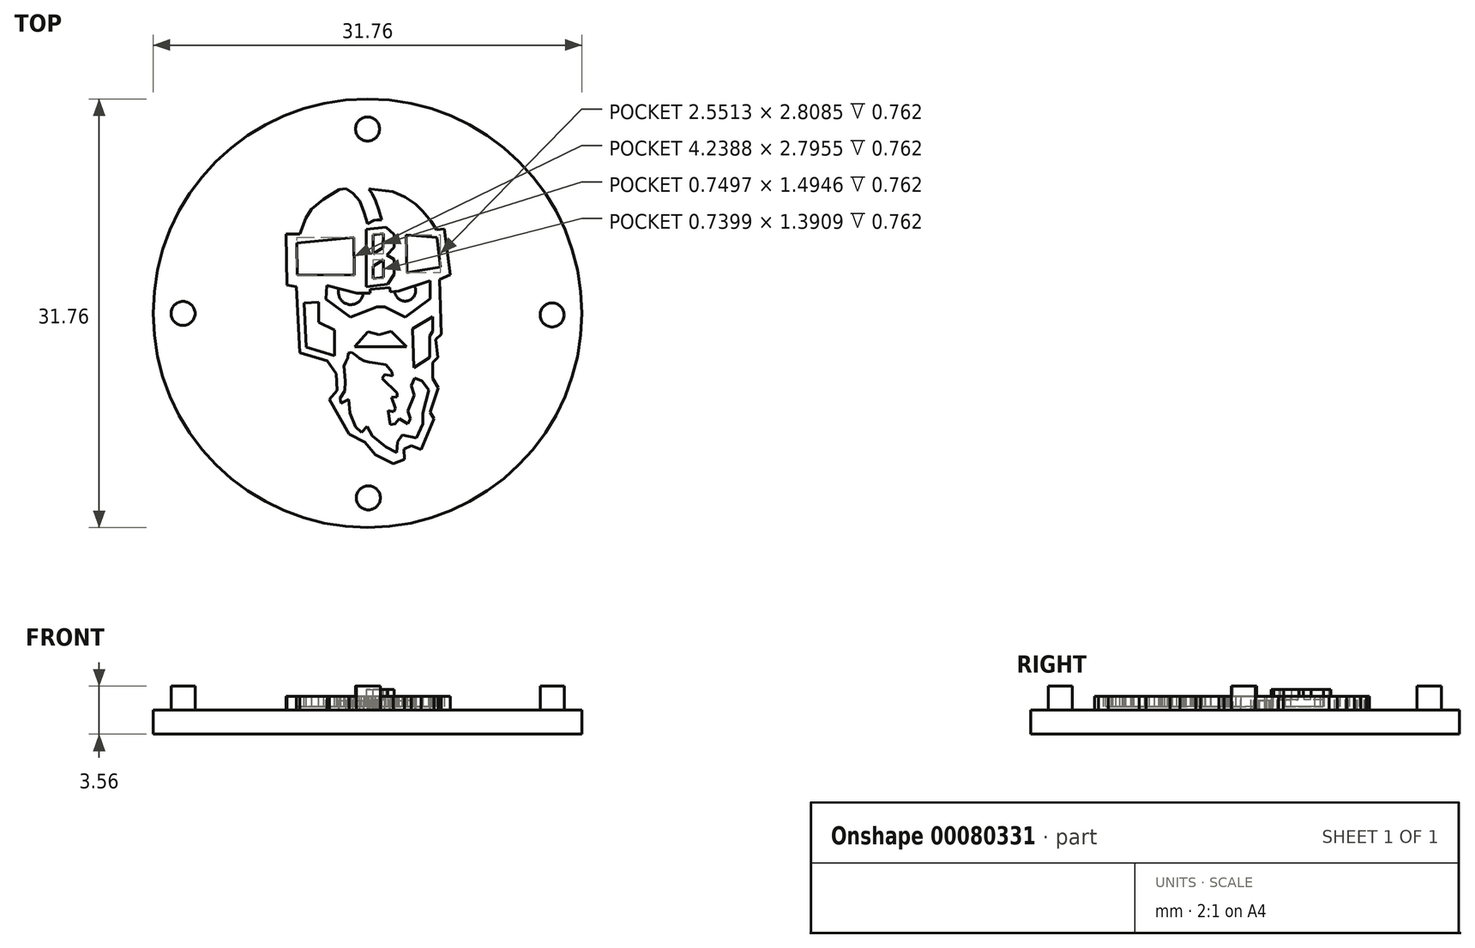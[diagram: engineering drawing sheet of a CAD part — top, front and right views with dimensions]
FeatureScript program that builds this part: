
annotation { "Feature Type Name" : "Feature", "Feature Type Description" : "" }
export const myFeature = defineFeature(function(context is Context, id is Id, definition is map)
    precondition{}
    {
        {
            var Q0;
            Q0=qCreatedBy(makeId("Top.planeOp"),FACE);
            var sketch = newSketch(context, id + "F0", { "sketchPlane" : qUnion([Q0])});
            skCircle(sketch, "E0", {"center": v(0, 0) * mm, "radius": 15.88 * mm});
            skSolve(sketch);
        }
        {
            var Q0;
            Q0=qSketchRegion(id+"F0",true);
            extrude(context, id + "F1", {"entities" : qUnion([Q0]), "oppositeDirection" : true, "depth" : 1.78 * mm});
        }
        {
            var Q0;
            Q0=makeQuery(id+"F1.opExtrude","CAP_FACE",FACE,{"disambiguationData":[OSD([sQuery(id+"F0.wireOp",EDGE,"E0")])],"isStart":true});
            var sketch = newSketch(context, id + "F2", { "sketchPlane" : qUnion([Q0])});
            skCircle(sketch, "E1", {"center": v(0, 0) * mm, "radius": 12.7 * mm});
            skSolve(sketch);
        }
        {
            var Q0;
            Q0=makeQuery(id+"F2.imprint","IMPRINT",FACE,{"disambiguationData":[TD([[makeQuery(id+"F2.imprint","IMPRINT",EDGE,{"derivedFrom":sQuery(id+"F2.wireOp",EDGE,"E1")}),-1.0]])]});
            var sketch = newSketch(context, id + "F3", { "sketchPlane" : qUnion([Q0])});
            skCircle(sketch, "E2", {"center": v(0, 13.65) * mm, "radius": 0.89 * mm});
            skCircle(sketch, "E3", {"center": v(-13.66, -0.02) * mm, "radius": 0.89 * mm});
            skCircle(sketch, "E4", {"center": v(0.06, -13.68) * mm, "radius": 0.89 * mm});
            skCircle(sketch, "E5", {"center": v(13.67, -0.12) * mm, "radius": 0.89 * mm});
            skSolve(sketch);
        }
        {
            var Q0;
            Q0=qSketchRegion(id+"F3",true);
            extrude(context, id + "F4", {"entities" : qUnion([Q0]), "operationType" : NewBodyOperationType.ADD, "depth" : 1.78 * mm});
        }
        {
            var Q0;
            Q0=makeQuery(id+"F2.imprint","IMPRINT",FACE,{"disambiguationData":[TD([[makeQuery(id+"F2.imprint","IMPRINT",EDGE,{"derivedFrom":sQuery(id+"F2.wireOp",EDGE,"E1")}),-1.0]])]});
            var sketch = newSketch(context, id + "F5", { "sketchPlane" : qUnion([Q0])});
            skLineSegment(sketch, "E6", {"start": v(-5.97, 2.09) * mm, "end": v(-6.04, 5.87) * mm});
            skLineSegment(sketch, "E7", {"start": v(-6.04, 5.87) * mm, "end": v(-5.01, 5.87) * mm});
            skLineSegment(sketch, "E8", {"start": v(-5.01, 5.87) * mm, "end": v(-4.57, 7.04) * mm});
            skLineSegment(sketch, "E9", {"start": v(-4.57, 7.04) * mm, "end": v(-4.15, 7.72) * mm});
            skLineSegment(sketch, "E10", {"start": v(-4.15, 7.72) * mm, "end": v(-3.26, 8.45) * mm});
            skLineSegment(sketch, "E11", {"start": v(-3.26, 8.45) * mm, "end": v(-2.1, 9.17) * mm});
            skLineSegment(sketch, "E12", {"start": v(-2.1, 9.17) * mm, "end": v(-1.1, 9.3) * mm});
            skLineSegment(sketch, "E13", {"start": v(-1.1, 9.3) * mm, "end": v(0.25, 9.2) * mm});
            skLineSegment(sketch, "E14", {"start": v(0.25, 9.2) * mm, "end": v(1.86, 9) * mm});
            skLineSegment(sketch, "E15", {"start": v(1.86, 9) * mm, "end": v(2.79, 8.58) * mm});
            skLineSegment(sketch, "E16", {"start": v(2.79, 8.58) * mm, "end": v(3.55, 8.1) * mm});
            skLineSegment(sketch, "E17", {"start": v(3.55, 8.1) * mm, "end": v(4.1, 7.55) * mm});
            skLineSegment(sketch, "E18", {"start": v(4.1, 7.55) * mm, "end": v(4.71, 6.83) * mm});
            skLineSegment(sketch, "E19", {"start": v(4.71, 6.83) * mm, "end": v(5.13, 6.18) * mm});
            skLineSegment(sketch, "E20", {"start": v(5.13, 6.18) * mm, "end": v(5.68, 6.25) * mm});
            skLineSegment(sketch, "E21", {"start": v(5.68, 6.25) * mm, "end": v(6.12, 2.84) * mm});
            skLineSegment(sketch, "E22", {"start": v(6.12, 2.84) * mm, "end": v(5.33, 2.5) * mm});
            skLineSegment(sketch, "E23", {"start": v(5.47, -1.56) * mm, "end": v(5.06, -1.93) * mm});
            skLineSegment(sketch, "E24", {"start": v(5.06, -1.93) * mm, "end": v(5.2, -3.27) * mm});
            skLineSegment(sketch, "E25", {"start": v(5.2, -3.27) * mm, "end": v(4.82, -3.65) * mm});
            skLineSegment(sketch, "E26", {"start": v(4.82, -3.65) * mm, "end": v(4.82, -4.82) * mm});
            skLineSegment(sketch, "E27", {"start": v(4.82, -4.82) * mm, "end": v(5.23, -5.54) * mm});
            skLineSegment(sketch, "E28", {"start": v(5.23, -5.54) * mm, "end": v(4.65, -7.33) * mm});
            skLineSegment(sketch, "E29", {"start": v(4.65, -7.33) * mm, "end": v(4.92, -7.81) * mm});
            skLineSegment(sketch, "E30", {"start": v(4.92, -7.81) * mm, "end": v(3.96, -10.11) * mm});
            skLineSegment(sketch, "E31", {"start": v(3.96, -10.11) * mm, "end": v(3.24, -9.8) * mm});
            skLineSegment(sketch, "E32", {"start": v(3.24, -9.8) * mm, "end": v(2.69, -10.08) * mm});
            skLineSegment(sketch, "E33", {"start": v(2.69, -10.08) * mm, "end": v(2.72, -10.84) * mm});
            skLineSegment(sketch, "E34", {"start": v(2.72, -10.84) * mm, "end": v(1.9, -11.15) * mm});
            skLineSegment(sketch, "E35", {"start": v(1.9, -11.15) * mm, "end": v(0.59, -10.5) * mm});
            skLineSegment(sketch, "E36", {"start": v(0.59, -10.5) * mm, "end": v(-0.2, -9.56) * mm});
            skLineSegment(sketch, "E37", {"start": v(-0.2, -9.56) * mm, "end": v(-1.37, -8.95) * mm});
            skLineSegment(sketch, "E38", {"start": v(-1.37, -8.95) * mm, "end": v(-2.81, -6.4) * mm});
            skLineSegment(sketch, "E39", {"start": v(-2.81, -6.4) * mm, "end": v(-2.26, -5.71) * mm});
            skLineSegment(sketch, "E40", {"start": v(-2.26, -5.71) * mm, "end": v(-2.33, -4.48) * mm});
            skLineSegment(sketch, "E41", {"start": v(-2.33, -4.48) * mm, "end": v(-2.98, -3.52) * mm});
            skLineSegment(sketch, "E42", {"start": v(-2.98, -3.52) * mm, "end": v(-5.01, -2.93) * mm});
            skLineSegment(sketch, "E43", {"start": v(-5.25, 1.95) * mm, "end": v(-5.97, 2.09) * mm});
            skLineSegment(sketch, "E44", {"start": v(-5.25, 1.95) * mm, "end": v(-5.01, -2.93) * mm});
            skLineSegment(sketch, "E45", {"start": v(5.33, 2.5) * mm, "end": v(5.47, -1.56) * mm});
            skSolve(sketch);
        }
        {
            var Q0;
            Q0=qSketchRegion(id+"F5",true);
            extrude(context, id + "F6", {"entities" : qUnion([Q0]), "operationType" : NewBodyOperationType.ADD, "depth" : 1.02 * mm});
        }
        {
            var Q0;
            Q0=makeQuery(id+"F6.opExtrude","CAP_FACE",FACE,{"disambiguationData":[OSD([sQuery(id+"F5.wireOp",EDGE,"E6"),sQuery(id+"F5.wireOp",EDGE,"E7"),sQuery(id+"F5.wireOp",EDGE,"E8"),sQuery(id+"F5.wireOp",EDGE,"E9"),sQuery(id+"F5.wireOp",EDGE,"E10"),sQuery(id+"F5.wireOp",EDGE,"E11"),sQuery(id+"F5.wireOp",EDGE,"E12"),sQuery(id+"F5.wireOp",EDGE,"E13"),sQuery(id+"F5.wireOp",EDGE,"E14"),sQuery(id+"F5.wireOp",EDGE,"E15"),sQuery(id+"F5.wireOp",EDGE,"E16"),sQuery(id+"F5.wireOp",EDGE,"E17"),sQuery(id+"F5.wireOp",EDGE,"E18"),sQuery(id+"F5.wireOp",EDGE,"E19"),sQuery(id+"F5.wireOp",EDGE,"E20"),sQuery(id+"F5.wireOp",EDGE,"E21"),sQuery(id+"F5.wireOp",EDGE,"E22"),sQuery(id+"F5.wireOp",EDGE,"E23"),sQuery(id+"F5.wireOp",EDGE,"E24"),sQuery(id+"F5.wireOp",EDGE,"E25"),sQuery(id+"F5.wireOp",EDGE,"E26"),sQuery(id+"F5.wireOp",EDGE,"E27"),sQuery(id+"F5.wireOp",EDGE,"E28"),sQuery(id+"F5.wireOp",EDGE,"E29"),sQuery(id+"F5.wireOp",EDGE,"E30"),sQuery(id+"F5.wireOp",EDGE,"E31"),sQuery(id+"F5.wireOp",EDGE,"E32"),sQuery(id+"F5.wireOp",EDGE,"E33"),sQuery(id+"F5.wireOp",EDGE,"E34"),sQuery(id+"F5.wireOp",EDGE,"E35"),sQuery(id+"F5.wireOp",EDGE,"E36"),sQuery(id+"F5.wireOp",EDGE,"E37"),sQuery(id+"F5.wireOp",EDGE,"E38"),sQuery(id+"F5.wireOp",EDGE,"E39"),sQuery(id+"F5.wireOp",EDGE,"E40"),sQuery(id+"F5.wireOp",EDGE,"E41"),sQuery(id+"F5.wireOp",EDGE,"E42"),sQuery(id+"F5.wireOp",EDGE,"E43"),sQuery(id+"F5.wireOp",EDGE,"E44"),sQuery(id+"F5.wireOp",EDGE,"E45")])],"isStart":false});
            var sketch = newSketch(context, id + "F7", { "sketchPlane" : qUnion([Q0])});
            skLineSegment(sketch, "E46", {"start": v(1.35, 6.38) * mm, "end": v(-0.1, 6.21) * mm});
            skLineSegment(sketch, "E47", {"start": v(-0.1, 6.21) * mm, "end": v(-0.1, 1.96) * mm});
            skLineSegment(sketch, "E48", {"start": v(1.99, 2.88) * mm, "end": v(1.99, 4) * mm});
            skLineSegment(sketch, "E49", {"start": v(1.98, 4.9) * mm, "end": v(1.98, 5.82) * mm});
            skLineSegment(sketch, "E50", {"start": v(1.98, 5.82) * mm, "end": v(1.35, 6.38) * mm});
            skLineSegment(sketch, "E51", {"start": v(1.99, 4) * mm, "end": v(1.44, 4.32) * mm});
            skLineSegment(sketch, "E52", {"start": v(1.44, 4.32) * mm, "end": v(1.98, 4.9) * mm});
            skLineSegment(sketch, "E53", {"start": v(-0.1, 1.96) * mm, "end": v(1.5, 2.15) * mm});
            skLineSegment(sketch, "E54", {"start": v(1.5, 2.15) * mm, "end": v(1.99, 2.88) * mm});
            skSolve(sketch);
        }
        {
            var Q0;
            Q0=qSketchRegion(id+"F7",true);
            extrude(context, id + "F8", {"entities" : qUnion([Q0]), "operationType" : NewBodyOperationType.ADD, "depth" : 0.5 * mm});
        }
        {
            var Q0;
            Q0=makeQuery(id+"F6.opExtrude","CAP_FACE",FACE,{"disambiguationData":[OSD([sQuery(id+"F5.wireOp",EDGE,"E6"),sQuery(id+"F5.wireOp",EDGE,"E7"),sQuery(id+"F5.wireOp",EDGE,"E8"),sQuery(id+"F5.wireOp",EDGE,"E9"),sQuery(id+"F5.wireOp",EDGE,"E10"),sQuery(id+"F5.wireOp",EDGE,"E11"),sQuery(id+"F5.wireOp",EDGE,"E12"),sQuery(id+"F5.wireOp",EDGE,"E13"),sQuery(id+"F5.wireOp",EDGE,"E14"),sQuery(id+"F5.wireOp",EDGE,"E15"),sQuery(id+"F5.wireOp",EDGE,"E16"),sQuery(id+"F5.wireOp",EDGE,"E17"),sQuery(id+"F5.wireOp",EDGE,"E18"),sQuery(id+"F5.wireOp",EDGE,"E19"),sQuery(id+"F5.wireOp",EDGE,"E20"),sQuery(id+"F5.wireOp",EDGE,"E21"),sQuery(id+"F5.wireOp",EDGE,"E22"),sQuery(id+"F5.wireOp",EDGE,"E23"),sQuery(id+"F5.wireOp",EDGE,"E24"),sQuery(id+"F5.wireOp",EDGE,"E25"),sQuery(id+"F5.wireOp",EDGE,"E26"),sQuery(id+"F5.wireOp",EDGE,"E27"),sQuery(id+"F5.wireOp",EDGE,"E28"),sQuery(id+"F5.wireOp",EDGE,"E29"),sQuery(id+"F5.wireOp",EDGE,"E30"),sQuery(id+"F5.wireOp",EDGE,"E31"),sQuery(id+"F5.wireOp",EDGE,"E32"),sQuery(id+"F5.wireOp",EDGE,"E33"),sQuery(id+"F5.wireOp",EDGE,"E34"),sQuery(id+"F5.wireOp",EDGE,"E35"),sQuery(id+"F5.wireOp",EDGE,"E36"),sQuery(id+"F5.wireOp",EDGE,"E37"),sQuery(id+"F5.wireOp",EDGE,"E38"),sQuery(id+"F5.wireOp",EDGE,"E39"),sQuery(id+"F5.wireOp",EDGE,"E40"),sQuery(id+"F5.wireOp",EDGE,"E41"),sQuery(id+"F5.wireOp",EDGE,"E42"),sQuery(id+"F5.wireOp",EDGE,"E43"),sQuery(id+"F5.wireOp",EDGE,"E44"),sQuery(id+"F5.wireOp",EDGE,"E45")])],"isStart":false});
            var sketch = newSketch(context, id + "F9", { "sketchPlane" : qUnion([Q0])});
            skLineSegment(sketch, "E55", {"start": v(-5.23, 5.2) * mm, "end": v(-5.2, 2.85) * mm});
            skLineSegment(sketch, "E56", {"start": v(-5.2, 2.85) * mm, "end": v(-1, 2.8) * mm});
            skLineSegment(sketch, "E57", {"start": v(-1, 2.8) * mm, "end": v(-1, 5.6) * mm});
            skLineSegment(sketch, "E58", {"start": v(-1, 5.6) * mm, "end": v(-5.23, 5.2) * mm});
            skLineSegment(sketch, "E59", {"start": v(2.86, 5.8) * mm, "end": v(5.14, 5.6) * mm});
            skLineSegment(sketch, "E60", {"start": v(5.14, 5.6) * mm, "end": v(5.41, 3.42) * mm});
            skLineSegment(sketch, "E61", {"start": v(5.41, 3.42) * mm, "end": v(2.93, 3) * mm});
            skLineSegment(sketch, "E62", {"start": v(2.93, 3) * mm, "end": v(2.86, 5.8) * mm});
            skSolve(sketch);
        }
        {
            var Q0;
            Q0=qSketchRegion(id+"F9",true);
            extrude(context, id + "F10", {"entities" : qUnion([Q0]), "operationType" : NewBodyOperationType.REMOVE, "oppositeDirection" : true, "depth" : 0.76 * mm});
        }
        {
            var Q0;
            Q0=makeQuery(id+"F6.opExtrude","CAP_FACE",FACE,{"disambiguationData":[OSD([sQuery(id+"F5.wireOp",EDGE,"E6"),sQuery(id+"F5.wireOp",EDGE,"E7"),sQuery(id+"F5.wireOp",EDGE,"E8"),sQuery(id+"F5.wireOp",EDGE,"E9"),sQuery(id+"F5.wireOp",EDGE,"E10"),sQuery(id+"F5.wireOp",EDGE,"E11"),sQuery(id+"F5.wireOp",EDGE,"E12"),sQuery(id+"F5.wireOp",EDGE,"E13"),sQuery(id+"F5.wireOp",EDGE,"E14"),sQuery(id+"F5.wireOp",EDGE,"E15"),sQuery(id+"F5.wireOp",EDGE,"E16"),sQuery(id+"F5.wireOp",EDGE,"E17"),sQuery(id+"F5.wireOp",EDGE,"E18"),sQuery(id+"F5.wireOp",EDGE,"E19"),sQuery(id+"F5.wireOp",EDGE,"E20"),sQuery(id+"F5.wireOp",EDGE,"E21"),sQuery(id+"F5.wireOp",EDGE,"E22"),sQuery(id+"F5.wireOp",EDGE,"E23"),sQuery(id+"F5.wireOp",EDGE,"E24"),sQuery(id+"F5.wireOp",EDGE,"E25"),sQuery(id+"F5.wireOp",EDGE,"E26"),sQuery(id+"F5.wireOp",EDGE,"E27"),sQuery(id+"F5.wireOp",EDGE,"E28"),sQuery(id+"F5.wireOp",EDGE,"E29"),sQuery(id+"F5.wireOp",EDGE,"E30"),sQuery(id+"F5.wireOp",EDGE,"E31"),sQuery(id+"F5.wireOp",EDGE,"E32"),sQuery(id+"F5.wireOp",EDGE,"E33"),sQuery(id+"F5.wireOp",EDGE,"E34"),sQuery(id+"F5.wireOp",EDGE,"E35"),sQuery(id+"F5.wireOp",EDGE,"E36"),sQuery(id+"F5.wireOp",EDGE,"E37"),sQuery(id+"F5.wireOp",EDGE,"E38"),sQuery(id+"F5.wireOp",EDGE,"E39"),sQuery(id+"F5.wireOp",EDGE,"E40"),sQuery(id+"F5.wireOp",EDGE,"E41"),sQuery(id+"F5.wireOp",EDGE,"E42"),sQuery(id+"F5.wireOp",EDGE,"E43"),sQuery(id+"F5.wireOp",EDGE,"E44"),sQuery(id+"F5.wireOp",EDGE,"E45")])],"isStart":false});
            var sketch = newSketch(context, id + "F11", { "sketchPlane" : qUnion([Q0])});
            skLineSegment(sketch, "E63", {"start": v(-3.03, 2.07) * mm, "end": v(-0.78, 1.48) * mm});
            skLineSegment(sketch, "E64", {"start": v(-0.78, 1.48) * mm, "end": v(0.2, 1.48) * mm});
            skLineSegment(sketch, "E65", {"start": v(0.2, 1.48) * mm, "end": v(0.2, 1.78) * mm});
            skLineSegment(sketch, "E66", {"start": v(0.2, 1.78) * mm, "end": v(1.65, 1.9) * mm});
            skLineSegment(sketch, "E67", {"start": v(1.65, 1.9) * mm, "end": v(1.68, 1.58) * mm});
            skLineSegment(sketch, "E68", {"start": v(1.68, 1.58) * mm, "end": v(2.32, 1.63) * mm});
            skLineSegment(sketch, "E69", {"start": v(2.32, 1.63) * mm, "end": v(4.64, 2.4) * mm});
            skLineSegment(sketch, "E70", {"start": v(4.64, 2.4) * mm, "end": v(4.64, 1.09) * mm});
            skLineSegment(sketch, "E71", {"start": v(4.64, 1.09) * mm, "end": v(2.8, -0.3) * mm});
            skLineSegment(sketch, "E72", {"start": v(2.8, -0.3) * mm, "end": v(1.27, 0.46) * mm});
            skLineSegment(sketch, "E73", {"start": v(0.7, 0.46) * mm, "end": v(-1.26, -0.3) * mm});
            skLineSegment(sketch, "E74", {"start": v(-1.26, -0.3) * mm, "end": v(-3.08, 1.04) * mm});
            skLineSegment(sketch, "E75", {"start": v(-3.08, 1.04) * mm, "end": v(-3.03, 2.07) * mm});
            skLineSegment(sketch, "E76", {"start": v(0.7, 0.46) * mm, "end": v(1.27, 0.46) * mm});
            skSolve(sketch);
        }
        {
            var Q0;
            Q0=qSketchRegion(id+"F11",true);
            extrude(context, id + "F12", {"entities" : qUnion([Q0]), "operationType" : NewBodyOperationType.REMOVE, "oppositeDirection" : true, "depth" : 1.02 * mm});
        }
        {
            var Q0;
            Q0=makeQuery(id+"F2.imprint","IMPRINT",FACE,{"disambiguationData":[TD([[makeQuery(id+"F2.imprint","IMPRINT",EDGE,{"derivedFrom":sQuery(id+"F2.wireOp",EDGE,"E1")}),1.0]])]});
            var sketch = newSketch(context, id + "F13", { "sketchPlane" : qUnion([Q0])});
            skLineSegment(sketch, "E77", {"start": v(-2.11, 1.83) * mm, "end": v(-0.78, 1.48) * mm});
            skLineSegment(sketch, "E78", {"start": v(-0.78, 1.48) * mm, "end": v(-0.32, 1.48) * mm});
            skArc(sketch, "E79", {"start": v(-2.11, 1.83) * mm, "mid": v(-1.41, 0.65) * mm, "end": v(-0.32, 1.48) * mm});
            skLineSegment(sketch, "E80", {"start": v(3.48, 2.02) * mm, "end": v(2.32, 1.63) * mm});
            skLineSegment(sketch, "E81", {"start": v(2.32, 1.63) * mm, "end": v(2.02, 1.6) * mm});
            skArc(sketch, "E82", {"start": v(2.02, 1.6) * mm, "mid": v(3, 0.92) * mm, "end": v(3.48, 2.02) * mm});
            skSolve(sketch);
        }
        {
            var Q0;
            Q0=qSketchRegion(id+"F13",true);
            extrude(context, id + "F14", {"entities" : qUnion([Q0]), "operationType" : NewBodyOperationType.ADD, "depth" : 0.71 * mm});
        }
        {
            var Q0;
            Q0=makeQuery(id+"F6.opExtrude","CAP_FACE",FACE,{"disambiguationData":[OSD([sQuery(id+"F5.wireOp",EDGE,"E6"),sQuery(id+"F5.wireOp",EDGE,"E7"),sQuery(id+"F5.wireOp",EDGE,"E8"),sQuery(id+"F5.wireOp",EDGE,"E9"),sQuery(id+"F5.wireOp",EDGE,"E10"),sQuery(id+"F5.wireOp",EDGE,"E11"),sQuery(id+"F5.wireOp",EDGE,"E12"),sQuery(id+"F5.wireOp",EDGE,"E13"),sQuery(id+"F5.wireOp",EDGE,"E14"),sQuery(id+"F5.wireOp",EDGE,"E15"),sQuery(id+"F5.wireOp",EDGE,"E16"),sQuery(id+"F5.wireOp",EDGE,"E17"),sQuery(id+"F5.wireOp",EDGE,"E18"),sQuery(id+"F5.wireOp",EDGE,"E19"),sQuery(id+"F5.wireOp",EDGE,"E20"),sQuery(id+"F5.wireOp",EDGE,"E21"),sQuery(id+"F5.wireOp",EDGE,"E22"),sQuery(id+"F5.wireOp",EDGE,"E23"),sQuery(id+"F5.wireOp",EDGE,"E24"),sQuery(id+"F5.wireOp",EDGE,"E25"),sQuery(id+"F5.wireOp",EDGE,"E26"),sQuery(id+"F5.wireOp",EDGE,"E27"),sQuery(id+"F5.wireOp",EDGE,"E28"),sQuery(id+"F5.wireOp",EDGE,"E29"),sQuery(id+"F5.wireOp",EDGE,"E30"),sQuery(id+"F5.wireOp",EDGE,"E31"),sQuery(id+"F5.wireOp",EDGE,"E32"),sQuery(id+"F5.wireOp",EDGE,"E33"),sQuery(id+"F5.wireOp",EDGE,"E34"),sQuery(id+"F5.wireOp",EDGE,"E35"),sQuery(id+"F5.wireOp",EDGE,"E36"),sQuery(id+"F5.wireOp",EDGE,"E37"),sQuery(id+"F5.wireOp",EDGE,"E38"),sQuery(id+"F5.wireOp",EDGE,"E39"),sQuery(id+"F5.wireOp",EDGE,"E40"),sQuery(id+"F5.wireOp",EDGE,"E41"),sQuery(id+"F5.wireOp",EDGE,"E42"),sQuery(id+"F5.wireOp",EDGE,"E43"),sQuery(id+"F5.wireOp",EDGE,"E44"),sQuery(id+"F5.wireOp",EDGE,"E45")])],"isStart":false});
            var sketch = newSketch(context, id + "F15", { "sketchPlane" : qUnion([Q0])});
            skLineSegment(sketch, "E83", {"start": v(-4.69, 0.77) * mm, "end": v(-4.52, -2.51) * mm});
            skLineSegment(sketch, "E84", {"start": v(-4.52, -2.51) * mm, "end": v(-2.46, -3.14) * mm});
            skLineSegment(sketch, "E85", {"start": v(-2.46, -3.14) * mm, "end": v(-2.46, -1.26) * mm});
            skLineSegment(sketch, "E86", {"start": v(-2.46, -1.26) * mm, "end": v(-3.63, -0.66) * mm});
            skLineSegment(sketch, "E87", {"start": v(-3.63, -0.66) * mm, "end": v(-3.63, 0.83) * mm});
            skLineSegment(sketch, "E88", {"start": v(-3.63, 0.83) * mm, "end": v(-4.69, 0.77) * mm});
            skLineSegment(sketch, "E89", {"start": v(4.84, -0.26) * mm, "end": v(4.84, -1.35) * mm});
            skLineSegment(sketch, "E90", {"start": v(4.84, -1.35) * mm, "end": v(4.6, -1.69) * mm});
            skLineSegment(sketch, "E91", {"start": v(4.6, -1.69) * mm, "end": v(4.6, -3.29) * mm});
            skLineSegment(sketch, "E92", {"start": v(4.6, -3.29) * mm, "end": v(3.44, -4.02) * mm});
            skLineSegment(sketch, "E93", {"start": v(3.34, -1.14) * mm, "end": v(4.84, -0.26) * mm});
            skLineSegment(sketch, "E94", {"start": v(3.34, -1.14) * mm, "end": v(3.44, -4.02) * mm});
            skSolve(sketch);
        }
        {
            var Q0;
            Q0=qSketchRegion(id+"F15",true);
            extrude(context, id + "F16", {"entities" : qUnion([Q0]), "operationType" : NewBodyOperationType.REMOVE, "oppositeDirection" : true, "depth" : 0.76 * mm});
        }
        {
            var Q0;
            Q0=makeQuery(id+"F6.opExtrude","CAP_FACE",FACE,{"disambiguationData":[OSD([sQuery(id+"F5.wireOp",EDGE,"E6"),sQuery(id+"F5.wireOp",EDGE,"E7"),sQuery(id+"F5.wireOp",EDGE,"E8"),sQuery(id+"F5.wireOp",EDGE,"E9"),sQuery(id+"F5.wireOp",EDGE,"E10"),sQuery(id+"F5.wireOp",EDGE,"E11"),sQuery(id+"F5.wireOp",EDGE,"E12"),sQuery(id+"F5.wireOp",EDGE,"E13"),sQuery(id+"F5.wireOp",EDGE,"E14"),sQuery(id+"F5.wireOp",EDGE,"E15"),sQuery(id+"F5.wireOp",EDGE,"E16"),sQuery(id+"F5.wireOp",EDGE,"E17"),sQuery(id+"F5.wireOp",EDGE,"E18"),sQuery(id+"F5.wireOp",EDGE,"E19"),sQuery(id+"F5.wireOp",EDGE,"E20"),sQuery(id+"F5.wireOp",EDGE,"E21"),sQuery(id+"F5.wireOp",EDGE,"E22"),sQuery(id+"F5.wireOp",EDGE,"E23"),sQuery(id+"F5.wireOp",EDGE,"E24"),sQuery(id+"F5.wireOp",EDGE,"E25"),sQuery(id+"F5.wireOp",EDGE,"E26"),sQuery(id+"F5.wireOp",EDGE,"E27"),sQuery(id+"F5.wireOp",EDGE,"E28"),sQuery(id+"F5.wireOp",EDGE,"E29"),sQuery(id+"F5.wireOp",EDGE,"E30"),sQuery(id+"F5.wireOp",EDGE,"E31"),sQuery(id+"F5.wireOp",EDGE,"E32"),sQuery(id+"F5.wireOp",EDGE,"E33"),sQuery(id+"F5.wireOp",EDGE,"E34"),sQuery(id+"F5.wireOp",EDGE,"E35"),sQuery(id+"F5.wireOp",EDGE,"E36"),sQuery(id+"F5.wireOp",EDGE,"E37"),sQuery(id+"F5.wireOp",EDGE,"E38"),sQuery(id+"F5.wireOp",EDGE,"E39"),sQuery(id+"F5.wireOp",EDGE,"E40"),sQuery(id+"F5.wireOp",EDGE,"E41"),sQuery(id+"F5.wireOp",EDGE,"E42"),sQuery(id+"F5.wireOp",EDGE,"E43"),sQuery(id+"F5.wireOp",EDGE,"E44"),sQuery(id+"F5.wireOp",EDGE,"E45")])],"isStart":false});
            var sketch = newSketch(context, id + "F17", { "sketchPlane" : qUnion([Q0])});
            skLineSegment(sketch, "E95", {"start": v(4.04, -5.02) * mm, "end": v(4.54, -5.68) * mm});
            skLineSegment(sketch, "E96", {"start": v(4.54, -5.68) * mm, "end": v(4.1, -7.4) * mm});
            skLineSegment(sketch, "E97", {"start": v(4.1, -7.4) * mm, "end": v(4.11, -8.2) * mm});
            skLineSegment(sketch, "E98", {"start": v(4.11, -8.2) * mm, "end": v(3.61, -9.25) * mm});
            skLineSegment(sketch, "E99", {"start": v(3.61, -9.25) * mm, "end": v(2.57, -9.04) * mm});
            skLineSegment(sketch, "E100", {"start": v(2.57, -9.04) * mm, "end": v(2.22, -9.54) * mm});
            skLineSegment(sketch, "E101", {"start": v(2.22, -9.54) * mm, "end": v(2.15, -10.3) * mm});
            skLineSegment(sketch, "E102", {"start": v(2.15, -10.3) * mm, "end": v(1.35, -9.9) * mm});
            skLineSegment(sketch, "E103", {"start": v(1.35, -9.9) * mm, "end": v(0.35, -9.07) * mm});
            skLineSegment(sketch, "E104", {"start": v(0.35, -9.07) * mm, "end": v(-0.03, -8.4) * mm});
            skLineSegment(sketch, "E105", {"start": v(-0.03, -8.4) * mm, "end": v(-0.44, -8.82) * mm});
            skLineSegment(sketch, "E106", {"start": v(-0.44, -8.82) * mm, "end": v(-0.9, -8.42) * mm});
            skLineSegment(sketch, "E107", {"start": v(-0.9, -8.42) * mm, "end": v(-1.3, -7.42) * mm});
            skLineSegment(sketch, "E108", {"start": v(-1.3, -7.42) * mm, "end": v(-1.4, -6.37) * mm});
            skLineSegment(sketch, "E109", {"start": v(-1.4, -6.37) * mm, "end": v(-1.98, -6.68) * mm});
            skLineSegment(sketch, "E110", {"start": v(-1.98, -6.68) * mm, "end": v(-2.02, -6.3) * mm});
            skLineSegment(sketch, "E111", {"start": v(-2.02, -6.3) * mm, "end": v(-1.7, -5.74) * mm});
            skLineSegment(sketch, "E112", {"start": v(-1.7, -5.74) * mm, "end": v(-1.65, -5.02) * mm});
            skLineSegment(sketch, "E113", {"start": v(-1.65, -5.02) * mm, "end": v(-1.75, -3.9) * mm});
            skLineSegment(sketch, "E114", {"start": v(0.56, -3.7) * mm, "end": v(1.37, -3.83) * mm});
            skLineSegment(sketch, "E115", {"start": v(1.37, -3.83) * mm, "end": v(1.82, -4.35) * mm});
            skLineSegment(sketch, "E116", {"start": v(1.82, -4.35) * mm, "end": v(1.84, -4.66) * mm});
            skLineSegment(sketch, "E117", {"start": v(1.84, -4.66) * mm, "end": v(1.26, -4.56) * mm});
            skLineSegment(sketch, "E118", {"start": v(1.26, -4.56) * mm, "end": v(1.08, -4.83) * mm});
            skLineSegment(sketch, "E119", {"start": v(1.08, -4.83) * mm, "end": v(2.18, -5.91) * mm});
            skLineSegment(sketch, "E120", {"start": v(2.18, -5.91) * mm, "end": v(2.2, -6.2) * mm});
            skLineSegment(sketch, "E121", {"start": v(2.2, -6.2) * mm, "end": v(1.78, -6.24) * mm});
            skLineSegment(sketch, "E122", {"start": v(1.78, -6.24) * mm, "end": v(2.07, -7.07) * mm});
            skLineSegment(sketch, "E123", {"start": v(2.07, -7.07) * mm, "end": v(1.95, -7.32) * mm});
            skLineSegment(sketch, "E124", {"start": v(1.95, -7.32) * mm, "end": v(1.53, -7.22) * mm});
            skLineSegment(sketch, "E125", {"start": v(1.53, -7.22) * mm, "end": v(1.68, -8.26) * mm});
            skLineSegment(sketch, "E126", {"start": v(1.68, -8.26) * mm, "end": v(2.03, -8.2) * mm});
            skLineSegment(sketch, "E127", {"start": v(2.03, -8.2) * mm, "end": v(2.36, -7.8) * mm});
            skLineSegment(sketch, "E128", {"start": v(3.5, -4.81) * mm, "end": v(4.04, -5.02) * mm});
            skLineSegment(sketch, "E129", {"start": v(3.2, -7.8) * mm, "end": v(3, -8.2) * mm});
            skLineSegment(sketch, "E130", {"start": v(3, -8.2) * mm, "end": v(2.36, -7.8) * mm});
            skLineSegment(sketch, "E131", {"start": v(3.2, -7.8) * mm, "end": v(3, -7.23) * mm});
            skLineSegment(sketch, "E132", {"start": v(3, -7.23) * mm, "end": v(3.46, -6.07) * mm});
            skLineSegment(sketch, "E133", {"start": v(3.46, -6.07) * mm, "end": v(3.23, -5.36) * mm});
            skLineSegment(sketch, "E134", {"start": v(3.23, -5.36) * mm, "end": v(3.5, -4.81) * mm});
            skLineSegment(sketch, "E135", {"start": v(0.56, -3.7) * mm, "end": v(0.14, -3.64) * mm});
            skLineSegment(sketch, "E136", {"start": v(0.14, -3.64) * mm, "end": v(-0.26, -3.52) * mm});
            skLineSegment(sketch, "E137", {"start": v(-0.26, -3.52) * mm, "end": v(-0.6, -3.32) * mm});
            skLineSegment(sketch, "E138", {"start": v(-0.6, -3.32) * mm, "end": v(-0.8, -3.15) * mm});
            skLineSegment(sketch, "E139", {"start": v(-0.8, -3.15) * mm, "end": v(-1.16, -2.9) * mm});
            skLineSegment(sketch, "E140", {"start": v(-1.16, -2.9) * mm, "end": v(-1.42, -2.94) * mm});
            skLineSegment(sketch, "E141", {"start": v(-1.42, -2.94) * mm, "end": v(-1.47, -3.32) * mm});
            skLineSegment(sketch, "E142", {"start": v(-1.47, -3.32) * mm, "end": v(-1.62, -3.63) * mm});
            skLineSegment(sketch, "E143", {"start": v(-1.62, -3.63) * mm, "end": v(-1.75, -3.9) * mm});
            skSolve(sketch);
        }
        {
            var Q0;
            Q0=qSketchRegion(id+"F17",true);
            extrude(context, id + "F18", {"entities" : qUnion([Q0]), "operationType" : NewBodyOperationType.REMOVE, "oppositeDirection" : true, "depth" : 0.76 * mm});
        }
        {
            var Q0;
            Q0=makeQuery(id+"F6.opExtrude","CAP_FACE",FACE,{"disambiguationData":[OSD([sQuery(id+"F5.wireOp",EDGE,"E6"),sQuery(id+"F5.wireOp",EDGE,"E7"),sQuery(id+"F5.wireOp",EDGE,"E8"),sQuery(id+"F5.wireOp",EDGE,"E9"),sQuery(id+"F5.wireOp",EDGE,"E10"),sQuery(id+"F5.wireOp",EDGE,"E11"),sQuery(id+"F5.wireOp",EDGE,"E12"),sQuery(id+"F5.wireOp",EDGE,"E13"),sQuery(id+"F5.wireOp",EDGE,"E14"),sQuery(id+"F5.wireOp",EDGE,"E15"),sQuery(id+"F5.wireOp",EDGE,"E16"),sQuery(id+"F5.wireOp",EDGE,"E17"),sQuery(id+"F5.wireOp",EDGE,"E18"),sQuery(id+"F5.wireOp",EDGE,"E19"),sQuery(id+"F5.wireOp",EDGE,"E20"),sQuery(id+"F5.wireOp",EDGE,"E21"),sQuery(id+"F5.wireOp",EDGE,"E22"),sQuery(id+"F5.wireOp",EDGE,"E23"),sQuery(id+"F5.wireOp",EDGE,"E24"),sQuery(id+"F5.wireOp",EDGE,"E25"),sQuery(id+"F5.wireOp",EDGE,"E26"),sQuery(id+"F5.wireOp",EDGE,"E27"),sQuery(id+"F5.wireOp",EDGE,"E28"),sQuery(id+"F5.wireOp",EDGE,"E29"),sQuery(id+"F5.wireOp",EDGE,"E30"),sQuery(id+"F5.wireOp",EDGE,"E31"),sQuery(id+"F5.wireOp",EDGE,"E32"),sQuery(id+"F5.wireOp",EDGE,"E33"),sQuery(id+"F5.wireOp",EDGE,"E34"),sQuery(id+"F5.wireOp",EDGE,"E35"),sQuery(id+"F5.wireOp",EDGE,"E36"),sQuery(id+"F5.wireOp",EDGE,"E37"),sQuery(id+"F5.wireOp",EDGE,"E38"),sQuery(id+"F5.wireOp",EDGE,"E39"),sQuery(id+"F5.wireOp",EDGE,"E40"),sQuery(id+"F5.wireOp",EDGE,"E41"),sQuery(id+"F5.wireOp",EDGE,"E42"),sQuery(id+"F5.wireOp",EDGE,"E43"),sQuery(id+"F5.wireOp",EDGE,"E44"),sQuery(id+"F5.wireOp",EDGE,"E45")])],"isStart":false});
            var sketch = newSketch(context, id + "F19", { "sketchPlane" : qUnion([Q0])});
            skLineSegment(sketch, "E144", {"start": v(-1.6, 9.24) * mm, "end": v(-1.1, 8.87) * mm});
            skLineSegment(sketch, "E145", {"start": v(-1.1, 8.87) * mm, "end": v(-0.57, 8.3) * mm});
            skLineSegment(sketch, "E146", {"start": v(-0.57, 8.3) * mm, "end": v(-0.25, 7.45) * mm});
            skLineSegment(sketch, "E147", {"start": v(-0.25, 7.45) * mm, "end": v(0, 6.64) * mm});
            skLineSegment(sketch, "E148", {"start": v(0, 6.64) * mm, "end": v(0.48, 6.9) * mm});
            skLineSegment(sketch, "E149", {"start": v(0.48, 6.9) * mm, "end": v(0.7, 6.93) * mm});
            skLineSegment(sketch, "E150", {"start": v(0.7, 6.93) * mm, "end": v(1.05, 6.91) * mm});
            skLineSegment(sketch, "E151", {"start": v(1.05, 6.91) * mm, "end": v(0.84, 7.67) * mm});
            skLineSegment(sketch, "E152", {"start": v(0.84, 7.67) * mm, "end": v(0.6, 8.32) * mm});
            skLineSegment(sketch, "E153", {"start": v(0.6, 8.32) * mm, "end": v(0.35, 8.84) * mm});
            skLineSegment(sketch, "E154", {"start": v(0.35, 8.84) * mm, "end": v(0.1, 9.21) * mm});
            skLineSegment(sketch, "E155", {"start": v(-1.6, 9.24) * mm, "end": v(-1.1, 9.3) * mm});
            skLineSegment(sketch, "E156", {"start": v(-1.1, 9.3) * mm, "end": v(0.1, 9.21) * mm});
            skSolve(sketch);
        }
        {
            var Q0;
            Q0=qSketchRegion(id+"F19",true);
            extrude(context, id + "F20", {"entities" : qUnion([Q0]), "operationType" : NewBodyOperationType.REMOVE, "oppositeDirection" : true, "depth" : 1.02 * mm});
        }
        {
            var Q0;
            Q0=makeQuery(id+"F6.opExtrude","CAP_FACE",FACE,{"disambiguationData":[OSD([sQuery(id+"F5.wireOp",EDGE,"E6"),sQuery(id+"F5.wireOp",EDGE,"E7"),sQuery(id+"F5.wireOp",EDGE,"E8"),sQuery(id+"F5.wireOp",EDGE,"E9"),sQuery(id+"F5.wireOp",EDGE,"E10"),sQuery(id+"F5.wireOp",EDGE,"E11"),sQuery(id+"F5.wireOp",EDGE,"E12"),sQuery(id+"F5.wireOp",EDGE,"E13"),sQuery(id+"F5.wireOp",EDGE,"E14"),sQuery(id+"F5.wireOp",EDGE,"E15"),sQuery(id+"F5.wireOp",EDGE,"E16"),sQuery(id+"F5.wireOp",EDGE,"E17"),sQuery(id+"F5.wireOp",EDGE,"E18"),sQuery(id+"F5.wireOp",EDGE,"E19"),sQuery(id+"F5.wireOp",EDGE,"E20"),sQuery(id+"F5.wireOp",EDGE,"E21"),sQuery(id+"F5.wireOp",EDGE,"E22"),sQuery(id+"F5.wireOp",EDGE,"E23"),sQuery(id+"F5.wireOp",EDGE,"E24"),sQuery(id+"F5.wireOp",EDGE,"E25"),sQuery(id+"F5.wireOp",EDGE,"E26"),sQuery(id+"F5.wireOp",EDGE,"E27"),sQuery(id+"F5.wireOp",EDGE,"E28"),sQuery(id+"F5.wireOp",EDGE,"E29"),sQuery(id+"F5.wireOp",EDGE,"E30"),sQuery(id+"F5.wireOp",EDGE,"E31"),sQuery(id+"F5.wireOp",EDGE,"E32"),sQuery(id+"F5.wireOp",EDGE,"E33"),sQuery(id+"F5.wireOp",EDGE,"E34"),sQuery(id+"F5.wireOp",EDGE,"E35"),sQuery(id+"F5.wireOp",EDGE,"E36"),sQuery(id+"F5.wireOp",EDGE,"E37"),sQuery(id+"F5.wireOp",EDGE,"E38"),sQuery(id+"F5.wireOp",EDGE,"E39"),sQuery(id+"F5.wireOp",EDGE,"E40"),sQuery(id+"F5.wireOp",EDGE,"E41"),sQuery(id+"F5.wireOp",EDGE,"E42"),sQuery(id+"F5.wireOp",EDGE,"E43"),sQuery(id+"F5.wireOp",EDGE,"E44"),sQuery(id+"F5.wireOp",EDGE,"E45")])],"isStart":false});
            var sketch = newSketch(context, id + "F21", { "sketchPlane" : qUnion([Q0])});
            skLineSegment(sketch, "E157", {"start": v(0.05, -1.38) * mm, "end": v(0.87, -1.6) * mm});
            skLineSegment(sketch, "E158", {"start": v(0.87, -1.6) * mm, "end": v(1.76, -1.33) * mm});
            skLineSegment(sketch, "E159", {"start": v(1.76, -1.33) * mm, "end": v(2.9, -2.48) * mm});
            skLineSegment(sketch, "E160", {"start": v(2.9, -2.48) * mm, "end": v(-0.96, -2.48) * mm});
            skLineSegment(sketch, "E161", {"start": v(-0.96, -2.48) * mm, "end": v(0.05, -1.38) * mm});
            skSolve(sketch);
        }
        {
            var Q0;
            Q0=qSketchRegion(id+"F21",true);
            extrude(context, id + "F22", {"entities" : qUnion([Q0]), "operationType" : NewBodyOperationType.REMOVE, "oppositeDirection" : true, "depth" : 0.76 * mm});
        }
        {
            var Q0;
            Q0=makeQuery(id+"F8.opExtrude","CAP_FACE",FACE,{"disambiguationData":[OSD([sQuery(id+"F7.wireOp",EDGE,"E46"),sQuery(id+"F7.wireOp",EDGE,"E47"),sQuery(id+"F7.wireOp",EDGE,"E48"),sQuery(id+"F7.wireOp",EDGE,"E49"),sQuery(id+"F7.wireOp",EDGE,"E50"),sQuery(id+"F7.wireOp",EDGE,"E51"),sQuery(id+"F7.wireOp",EDGE,"E52"),sQuery(id+"F7.wireOp",EDGE,"E53"),sQuery(id+"F7.wireOp",EDGE,"E54")])],"isStart":false});
            var sketch = newSketch(context, id + "F23", { "sketchPlane" : qUnion([Q0])});
            skLineSegment(sketch, "E162", {"start": v(1.17, 3.96) * mm, "end": v(0.43, 3.47) * mm});
            skLineSegment(sketch, "E163", {"start": v(0.43, 2.56) * mm, "end": v(1.17, 2.66) * mm});
            skLineSegment(sketch, "E164", {"start": v(1.17, 2.66) * mm, "end": v(1.17, 3.96) * mm});
            skLineSegment(sketch, "E165", {"start": v(1.16, 4.86) * mm, "end": v(0.43, 4.4) * mm});
            skLineSegment(sketch, "E166", {"start": v(0.43, 5.8) * mm, "end": v(1.18, 5.9) * mm});
            skLineSegment(sketch, "E167", {"start": v(1.18, 5.9) * mm, "end": v(1.16, 4.86) * mm});
            skLineSegment(sketch, "E168", {"start": v(0.43, 5.8) * mm, "end": v(0.43, 4.4) * mm});
            skLineSegment(sketch, "E169", {"start": v(0.43, 3.47) * mm, "end": v(0.43, 2.56) * mm});
            skSolve(sketch);
        }
        {
            var Q0;
            Q0 = qSketchRegion(id + "F23", true);
            extrude(context, id + "F24", {"entities" : qUnion([Q0]), "operationType" : NewBodyOperationType.REMOVE, "oppositeDirection" : true, "depth" : 0.76 * mm});
        }
    });
